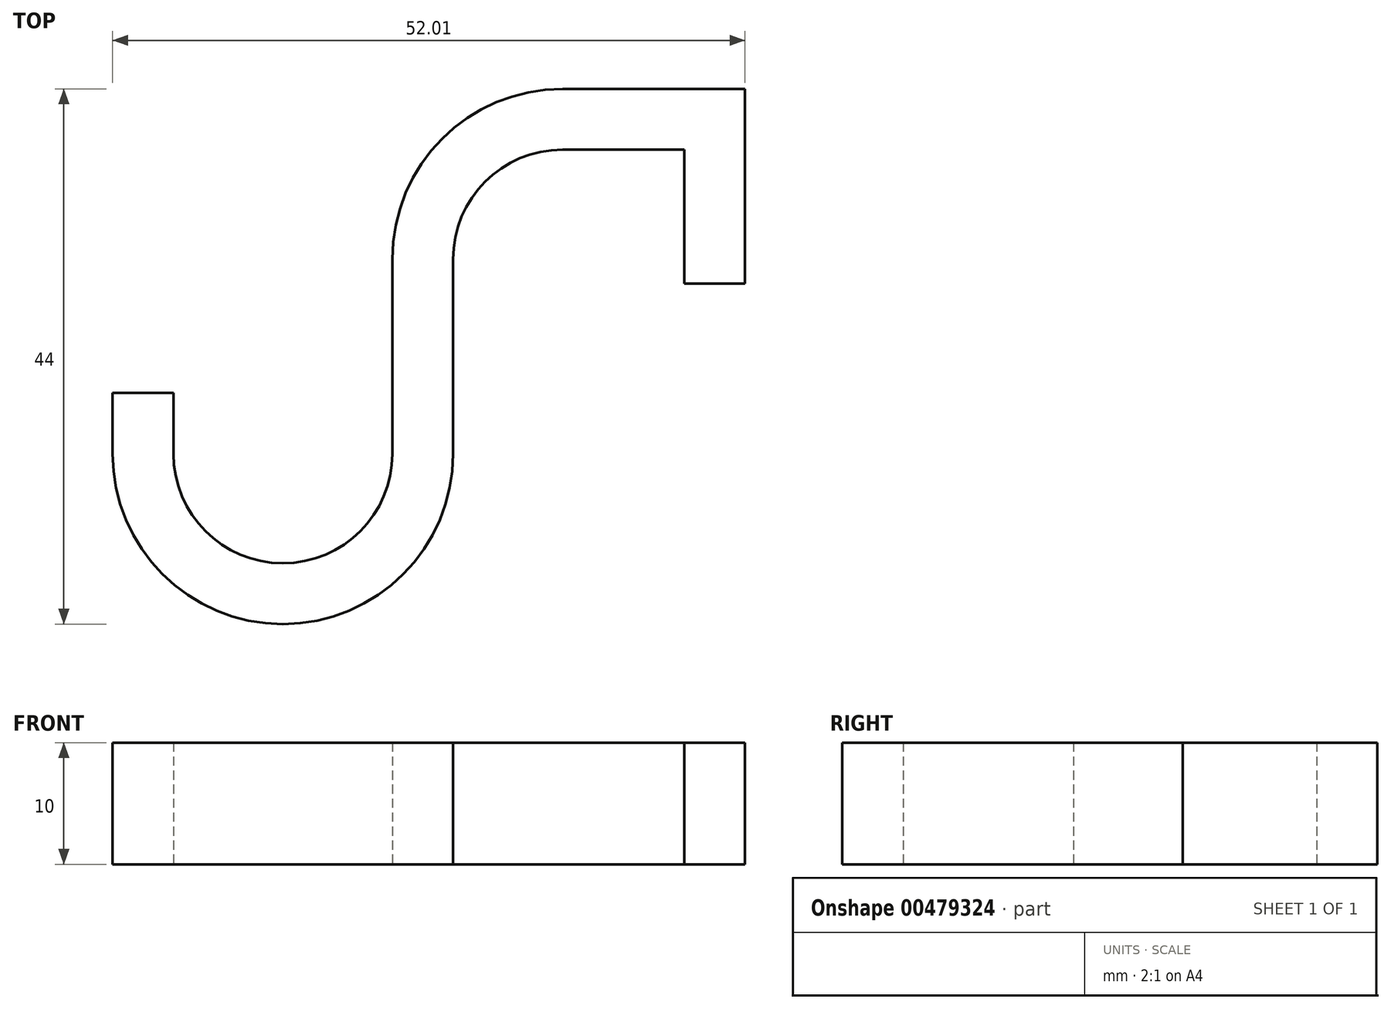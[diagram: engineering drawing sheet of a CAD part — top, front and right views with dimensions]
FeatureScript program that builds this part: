
annotation { "Feature Type Name" : "Feature", "Feature Type Description" : "" }
export const myFeature = defineFeature(function(context is Context, id is Id, definition is map)
    precondition{}
    {
        {
            var Q0;
            Q0=qCreatedBy(makeId("Top.planeOp"),FACE);
            var sketch = newSketch(context, id + "F0", { "sketchPlane" : qUnion([Q0])});
            skLineSegment(sketch, "E0", {"start": v(9.93, 5.09) * mm, "end": v(9.93, -10.91) * mm});
            skArc(sketch, "E1", {"start": v(-8.07, -10.91) * mm, "mid": v(0.93, -19.91) * mm, "end": v(9.93, -10.91) * mm});
            skLineSegment(sketch, "E2", {"start": v(-8.07, -10.91) * mm, "end": v(-8.07, -5.91) * mm});
            skLineSegment(sketch, "E3", {"start": v(23.93, 19.09) * mm, "end": v(38.93, 19.09) * mm});
            skLineSegment(sketch, "E4", {"start": v(38.93, 19.09) * mm, "end": v(38.93, 9.09) * mm});
            skPoint(sketch, "E5.visualSharp", {"position": v(9.93, 19.09) * mm});
            skArc(sketch, "E5.filletArc", {"start": v(23.93, 19.09) * mm, "mid": v(14.03, 14.99) * mm, "end": v(9.93, 5.09) * mm});
            skLineSegment(sketch, "E6.0", {"start": v(-13.07, -10.91) * mm, "end": v(-13.07, -5.91) * mm});
            skLineSegment(sketch, "E6.1", {"start": v(33.93, 14.09) * mm, "end": v(33.93, 3.09) * mm});
            skLineSegment(sketch, "E6.2", {"start": v(23.93, 14.09) * mm, "end": v(33.93, 14.09) * mm});
            skLineSegment(sketch, "E6.3", {"start": v(14.93, 5.09) * mm, "end": v(14.93, -10.91) * mm});
            skArc(sketch, "E6.4", {"start": v(-13.07, -10.91) * mm, "mid": v(0.93, -24.91) * mm, "end": v(14.93, -10.91) * mm});
            skLineSegment(sketch, "E7", {"start": v(-13.07, -5.91) * mm, "end": v(-8.07, -5.91) * mm});
            skPoint(sketch, "E8.visualSharp", {"position": v(14.93, 14.09) * mm});
            skArc(sketch, "E8.filletArc", {"start": v(23.93, 14.09) * mm, "mid": v(17.57, 11.45) * mm, "end": v(14.93, 5.09) * mm});
            skLineSegment(sketch, "E9", {"start": v(33.93, 3.09) * mm, "end": v(38.94, 3.09) * mm});
            skLineSegment(sketch, "E10", {"start": v(38.94, 3.09) * mm, "end": v(38.93, 9.09) * mm});
            skLineSegment(sketch, "E11", {"start": v(23.93, 14.09) * mm, "end": v(23.93, 46) * mm, "construction": true});
            skSolve(sketch);
        }
        {
            var Q0;
            Q0 = qSketchRegion(id + "F0", true);
            extrude(context, id + "F1", {"entities" : qUnion([Q0]), "depth" : 10 * mm});
        }
    });
